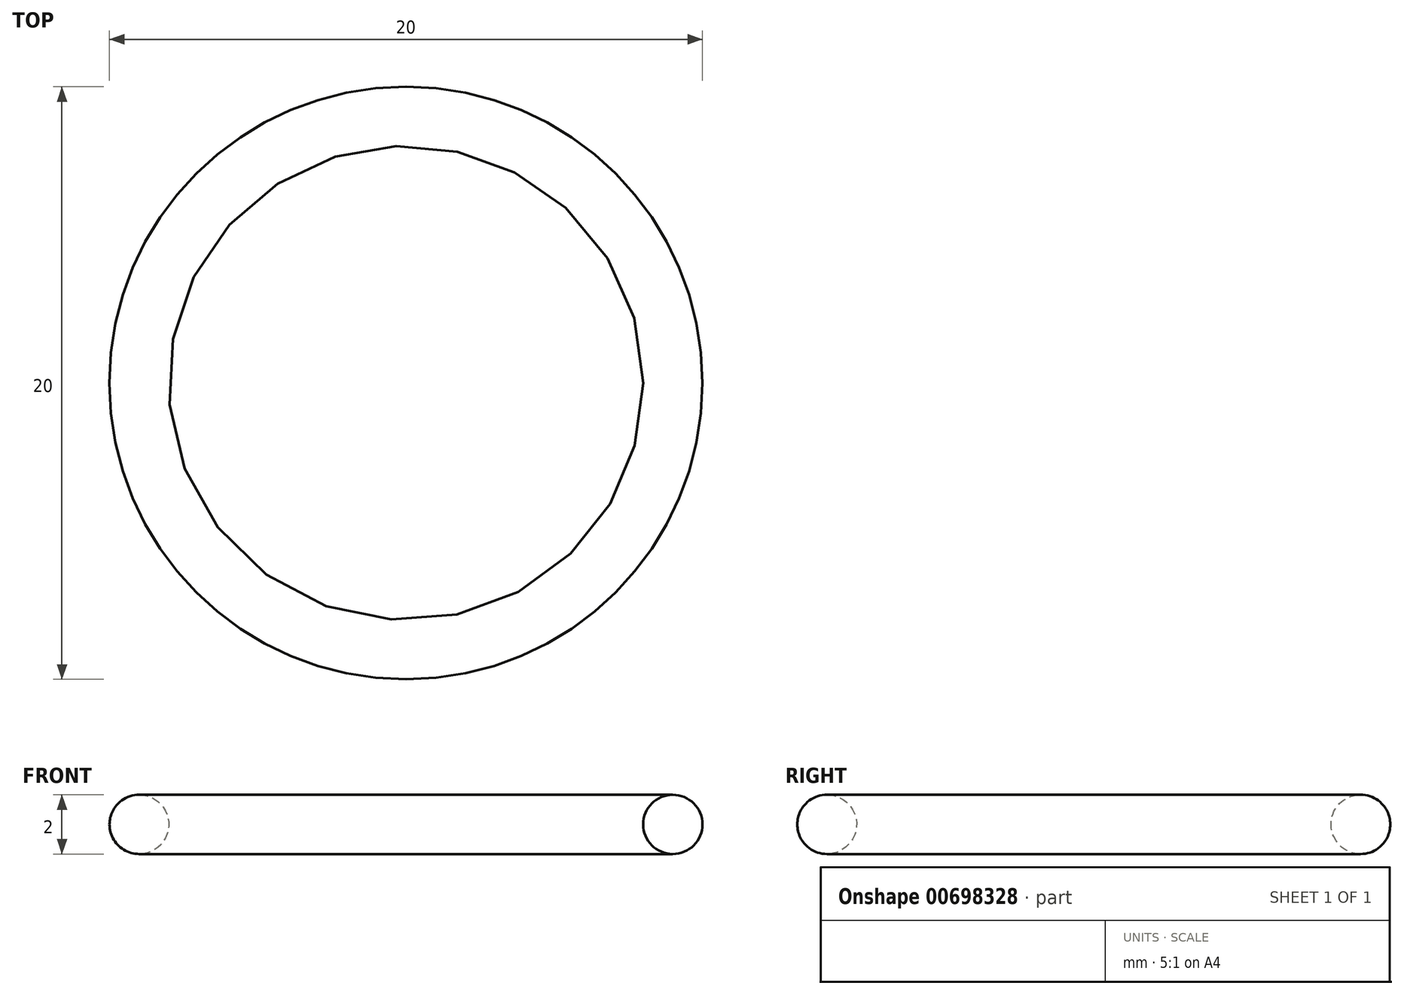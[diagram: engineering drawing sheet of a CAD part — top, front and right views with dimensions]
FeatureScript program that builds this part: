
annotation { "Feature Type Name" : "Feature", "Feature Type Description" : "" }
export const myFeature = defineFeature(function(context is Context, id is Id, definition is map)
    precondition{}
    {
        {
            var Q0;
            Q0=qCreatedBy(makeId("Top.planeOp"),FACE);
            var sketch = newSketch(context, id + "F0", { "sketchPlane" : qUnion([Q0])});
            skCircle(sketch, "E0", {"center": v(0, 0) * mm, "radius": 9 * mm});
            skSolve(sketch);
        }
        {
            var Q0;
            Q0=qCreatedBy(makeId("Right.planeOp"),FACE);
            var sketch = newSketch(context, id + "F1", { "sketchPlane" : qUnion([Q0])});
            skLineSegment(sketch, "E1.0", {"start": v(-9, 0) * mm, "end": v(9, 0) * mm, "construction": true});
            skCircle(sketch, "E2", {"center": v(-9, 0) * mm, "radius": 1 * mm});
            skSolve(sketch);
        }
        {
            var Q0;
            Q0=makeQuery(id+"F1.imprint","IMPRINT",FACE,{"disambiguationData":[TD([[makeQuery(id+"F1.imprint","IMPRINT",EDGE,{"derivedFrom":sQuery(id+"F1.wireOp",EDGE,"E2")}),1.0]])]});
            var Q1;
            Q1=sQuery(id+"F0.wireOp",EDGE,"E0");
            sweep(context, id + "F2", {"profiles" : qUnion([Q0]), "path" : qUnion([Q1])});
        }
    });
